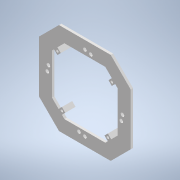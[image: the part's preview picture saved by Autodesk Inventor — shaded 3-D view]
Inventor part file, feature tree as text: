
AUTODESK INVENTOR PART (.ipt)
format: ipt  version: 2021.2 (Build 252289000, 289)  size: 217,600 bytes
history: native  units: mm
features: other x4, extrude x3, sketch x2, reference x1, projected_geometry x1
ambient origin geometry x8: Origin, YZ Plane, XZ Plane, XY Plane, X Axis, Y Axis, Z Axis, Center Point
bodies: Body1 (feature_tree)
feature tree (11):
  extrude  "Выдавливание2"  Depth=11.0mm
  other  "РабПлоскость1"
  extrude  "Выдавливание3"  Depth=11.0mm
  extrude  "Выдавливание4"  Depth=3.0mm
  sketch  "Эскиз1"
  reference  "Ссылка1"
  projected_geometry  "Спроецированная петля1"
  sketch  "Эскиз3"
  parser-record x1  (decoder bookkeeping rows leaked as tree rows — omitted from the tree; the rows remain in map.json)
  other  "Сборка1.iam"
  other  "Низ:1"
note: 1 file-system path scrubbed to <path> (originals preserved in map.json)
